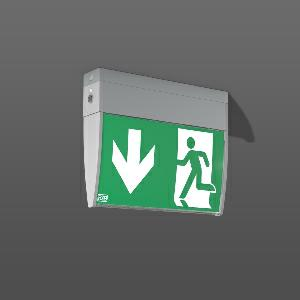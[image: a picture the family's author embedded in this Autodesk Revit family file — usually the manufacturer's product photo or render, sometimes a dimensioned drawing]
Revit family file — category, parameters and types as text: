
# Revit family: gsun_d_671996_004_2_def1
name_source: partatom
category: Lighting Fixtures
units: mm (PartAtom-declared; Revit-internal decimal feet)

## family parameters
Cut with Voids When Loaded = No
Host = Face
Light Source = No
Part Type = Normal
Room Calculation Point = No
Round Connector Dimension = Use Diameter
Shared = No

## types (1)
- GSUN D
    Apparent Load = 0 VA
    Default Elevation = 1800 mm
    Description = Series: GSUN D
Luminaire for escape route identification. Housing: extruded aluminium profile, powder-coated. 4 legends and 1 white lay in plastic sheet included. Universal mounting kit for ceiling and wall surface mounting. Driver integrated. Suitable for connection to central battery systems. 
Colour: silver
Length: 247 mm
Width: 45 mm
Height: 200 mm
Weight: 1 kg
Operating mode: maintained power mode
Viewing Distance: 24 m
Lamp: LED
Socket: without socket
Colour temperature: 4000K
System power: 3.7 W
System power, emergency: 3.7 W
Control gear: Converter not necessary
Protection class: I
Type of protection: IP 30
    Height = 200 mm  [stored 0.656168 ft]
    Lamp = 0 x
    Length = 247 mm
    Luminous efficacy = 0 lm/W
    Manufacturer = RZB
    ModVariant = No
    Model = 671996.004.2
    Mounting Place = Ceiling, Wall
    Mounting Type = Surface mounted
    Number of Poles = 1
    OnlyDefault = Yes
    Power Factor = 1
    Product Name = GSUN D
    Product group = Surface mounted ceiling and wall luminaires
    ProductGroupID = 305
    Protection Class = Protection class I
    Protection Degree = IP 30
    RLX_Detail_Level = 1
    RLX_Emergency_Light_Flux = 0 lm
    RLX_Emergency_Type = 0
    RLX_Emergency_Type_DB = No
    RlxData = <blob elided: 30237 chars, md5=76b83bce>
    Standby Power = 0 W
    System Light Flux = 0 lm
    System Power = 0 W
    Type Comments = Product without accessories
    Type Image = 671995.004.1.jpg
    URL = http://relux.com
    VarID = ---
    Voltage = 230 V
    Voltage Range = 220-240 V
    Weight = 0.00 kg
    Width = 45 mm

note: [stored X ft] marks values corroborated as IEEE doubles in the binary element streams (Revit-internal decimal feet)

## geometry (parser evidence)
native form markers: Blend x4, Sweep x9
no freeform markers — native parametric forms only
